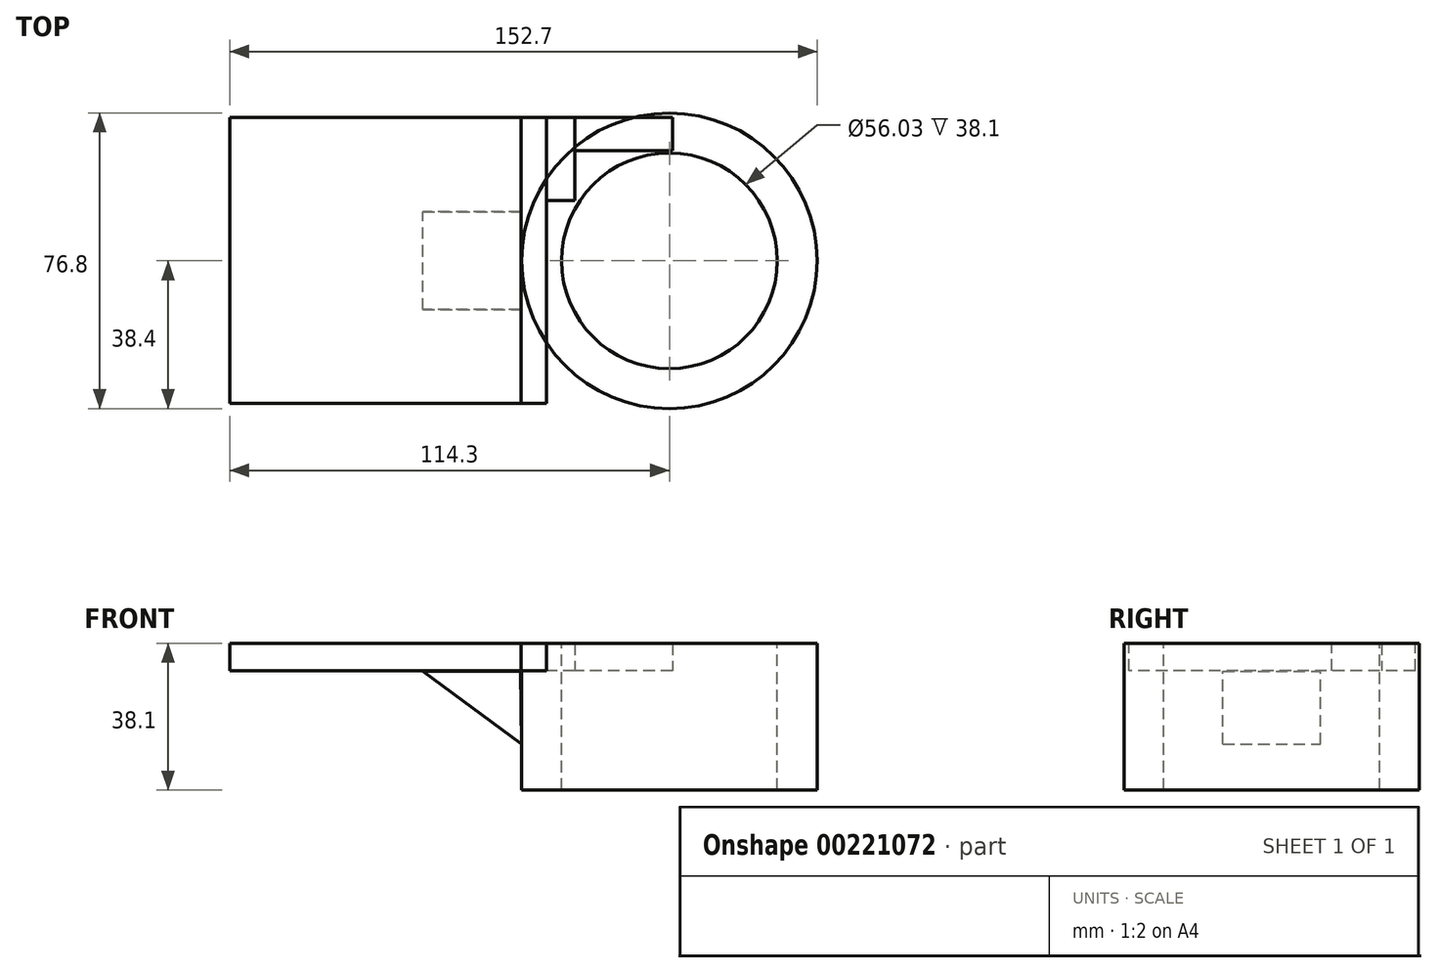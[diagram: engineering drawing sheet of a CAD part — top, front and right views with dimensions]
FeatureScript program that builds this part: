
annotation { "Feature Type Name" : "Feature", "Feature Type Description" : "" }
export const myFeature = defineFeature(function(context is Context, id is Id, definition is map)
    precondition{}
    {
        {
            var Q0;
            Q0=qCreatedBy(makeId("Top.planeOp"),FACE);
            var sketch = newSketch(context, id + "F0", { "sketchPlane" : qUnion([Q0])});
            skCircle(sketch, "E0", {"center": v(0, 0) * mm, "radius": 38.4 * mm});
            skSolve(sketch);
        }
        {
            var Q0;
            Q0 = qSketchRegion(id + "F0", true);
            extrude(context, id + "F1", {"entities" : qUnion([Q0]), "depth" : 38.1 * mm});
        }
        {
            var Q0;
            Q0=makeQuery(id+"F1.opExtrude","CAP_FACE",FACE,{"disambiguationData":[OSD([sQuery(id+"F0.wireOp",EDGE,"E0")])],"isStart":false});
            var sketch = newSketch(context, id + "F2", { "sketchPlane" : qUnion([Q0])});
            skCircle(sketch, "E1", {"center": v(0, 0) * mm, "radius": 28.02 * mm});
            skSolve(sketch);
        }
        {
            var Q0;
            Q0=makeQuery(id+"F1.opExtrude","CAP_FACE",FACE,{"disambiguationData":[OSD([sQuery(id+"F0.wireOp",EDGE,"E0")])],"isStart":false});
            var sketch = newSketch(context, id + "F3", { "sketchPlane" : qUnion([Q0])});
            skLineSegment(sketch, "E2.bottom", {"start": v(-114.3, 37.3) * mm, "end": v(-38.56, 37.3) * mm});
            skLineSegment(sketch, "E2.top", {"start": v(-114.3, -37.06) * mm, "end": v(-38.56, -37.06) * mm});
            skLineSegment(sketch, "E2.left", {"start": v(-114.3, 37.3) * mm, "end": v(-114.3, -37.06) * mm});
            skLineSegment(sketch, "E2.right", {"start": v(-38.56, 37.3) * mm, "end": v(-38.56, -37.06) * mm});
            skSolve(sketch);
        }
        {
            var Q0;
            Q0=makeQuery(id+"F3.imprint","IMPRINT",FACE,{"disambiguationData":[TD([[makeQuery(id+"F3.imprint","IMPRINT",EDGE,{"derivedFrom":sQuery(id+"F3.wireOp",EDGE,"E2.bottom")}),-1.0]])]});
            extrude(context, id + "F4", {"entities" : qUnion([Q0]), "oppositeDirection" : true, "depth" : 7.11 * mm});
        }
        {
            var Q0;
            Q0=makeQuery(id+"F2.imprint","IMPRINT",FACE,{"disambiguationData":[TD([[makeQuery(id+"F2.imprint","IMPRINT",EDGE,{"derivedFrom":sQuery(id+"F2.wireOp",EDGE,"E1")}),1.0]])]});
            var Q1;
            Q1=sQuery(id+"F2.wireOp",EDGE,"E1");
            extrude(context, id + "F5", {"entities" : qUnion([Q0]), "operationType" : NewBodyOperationType.REMOVE, "surfaceEntities" : qUnion([Q1]), "oppositeDirection" : true, "depth" : 75.44 * mm});
        }
        {
            var Q0;
            Q0=qCreatedBy(makeId("Front.planeOp"),FACE);
            var sketch = newSketch(context, id + "F6", { "sketchPlane" : qUnion([Q0])});
            skLineSegment(sketch, "E3", {"start": v(-38.68, 30.83) * mm, "end": v(-64.08, 30.83) * mm});
            skLineSegment(sketch, "E4", {"start": v(-64.08, 30.83) * mm, "end": v(-38.45, 11.9) * mm});
            skLineSegment(sketch, "E5", {"start": v(-38.45, 11.9) * mm, "end": v(-38.68, 30.83) * mm});
            skSolve(sketch);
        }
        {
            var Q0;
            Q0 = qSketchRegion(id + "F6", true);
            extrude(context, id + "F7", {"entities" : qUnion([Q0]), "endBound" : BoundingType.SYMMETRIC, "depth" : 25.4 * mm});
        }
        {
            var Q0;
            Q0=makeQuery(id+"F4.opExtrude","SWEPT_FACE",FACE,{"disambiguationData":[OSD([sQuery(id+"F3.wireOp",EDGE,"E2.right")])]});
            var sketch = newSketch(context, id + "F8", { "sketchPlane" : qUnion([Q0])});
            skSolve(sketch);
        }
        {
            var Q0;
            {var subQ0=sQuery(id+"F3.wireOp",EDGE,"E2.right");Q0=makeQuery(id+"F8.imprint","IMPRINT",FACE,{"disambiguationData":[TD([[makeQuery(id+"F8.imprint","IMPRINT",EDGE,{"derivedFrom":makeQuery(id+"F4.opExtrude","CAP_EDGE",EDGE,{"disambiguationData":[OSD([subQ0])],"isStart":true})}),1.0]])]});}
            extrude(context, id + "F9", {"entities" : qUnion([Q0]), "depth" : 6.6 * mm});
        }
        {
            var Q0;
            Q0=makeQuery(id+"F9.opExtrude","CAP_FACE",FACE,{"disambiguationData":[OSD([sQuery(id+"F3.wireOp",EDGE,"E2.bottom"),sQuery(id+"F3.wireOp",EDGE,"E2.top"),sQuery(id+"F3.wireOp",EDGE,"E2.right")])],"isStart":false});
            var sketch = newSketch(context, id + "F10", { "sketchPlane" : qUnion([Q0])});
            skLineSegment(sketch, "E6.bottom", {"start": v(37.3, 30.99) * mm, "end": v(15.66, 30.99) * mm});
            skLineSegment(sketch, "E6.top", {"start": v(37.3, 38.1) * mm, "end": v(15.66, 38.1) * mm});
            skLineSegment(sketch, "E6.left", {"start": v(37.3, 30.99) * mm, "end": v(37.3, 38.1) * mm});
            skLineSegment(sketch, "E6.right", {"start": v(15.66, 30.99) * mm, "end": v(15.66, 38.1) * mm});
            skSolve(sketch);
        }
        {
            var Q0;
            Q0 = qSketchRegion(id + "F10", true);
            extrude(context, id + "F11", {"entities" : qUnion([Q0]), "depth" : 7.37 * mm});
        }
        {
            var Q0;
            Q0=makeQuery(id+"F11.opExtrude","CAP_FACE",FACE,{"disambiguationData":[OSD([sQuery(id+"F10.wireOp",EDGE,"E6.bottom"),sQuery(id+"F10.wireOp",EDGE,"E6.top"),sQuery(id+"F10.wireOp",EDGE,"E6.left"),sQuery(id+"F10.wireOp",EDGE,"E6.right")])],"isStart":false});
            var sketch = newSketch(context, id + "F12", { "sketchPlane" : qUnion([Q0])});
            skLineSegment(sketch, "E7.bottom", {"start": v(37.3, 38.1) * mm, "end": v(28.63, 38.1) * mm});
            skLineSegment(sketch, "E7.top", {"start": v(37.3, 30.99) * mm, "end": v(28.63, 30.99) * mm});
            skLineSegment(sketch, "E7.left", {"start": v(37.3, 38.1) * mm, "end": v(37.3, 30.99) * mm});
            skLineSegment(sketch, "E7.right", {"start": v(28.63, 38.1) * mm, "end": v(28.63, 30.99) * mm});
            skSolve(sketch);
        }
        {
            var Q0;
            Q0 = qSketchRegion(id + "F12", true);
            extrude(context, id + "F13", {"entities" : qUnion([Q0]), "depth" : 25.4 * mm});
        }
    });
